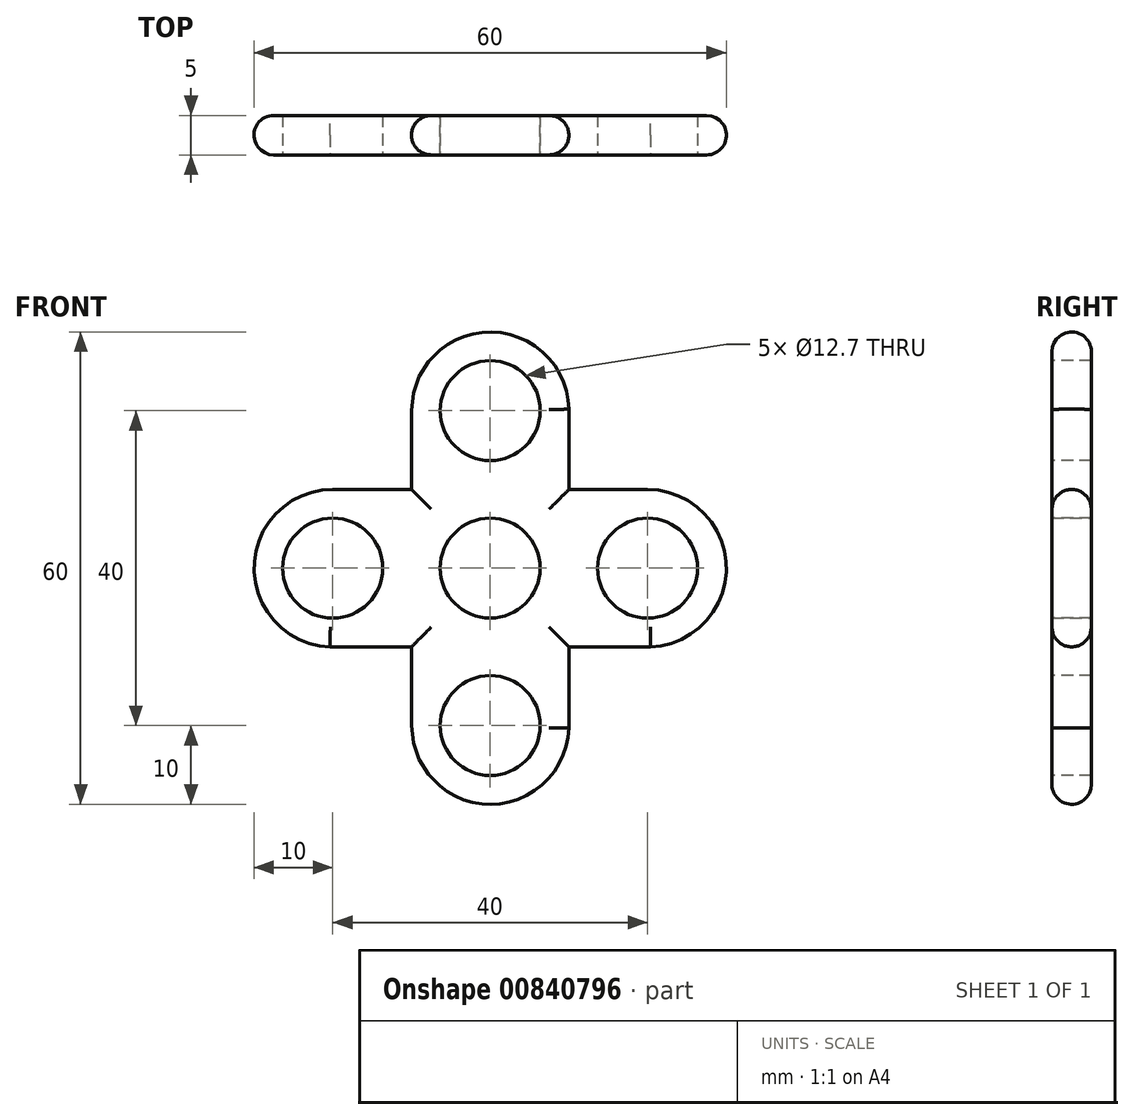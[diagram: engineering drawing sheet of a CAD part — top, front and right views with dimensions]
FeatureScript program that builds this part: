
annotation { "Feature Type Name" : "Feature", "Feature Type Description" : "" }
export const myFeature = defineFeature(function(context is Context, id is Id, definition is map)
    precondition{}
    {
        {
            var Q0;
            Q0=qCreatedBy(makeId("Front.planeOp"),FACE);
            var sketch = newSketch(context, id + "F0", { "sketchPlane" : qUnion([Q0])});
            skCircle(sketch, "E0", {"center": v(0, 0) * mm, "radius": 10 * mm});
            skCircle(sketch, "E1", {"center": v(0, 0) * mm, "radius": 6.35 * mm});
            skSolve(sketch);
        }
        {
            var Q0;
            Q0=makeQuery(id+"F0.imprint","IMPRINT",FACE,{"disambiguationData":[TD([[makeQuery(id+"F0.imprint","IMPRINT",EDGE,{"derivedFrom":sQuery(id+"F0.wireOp",EDGE,"E0")}),1.0]])]});
            extrude(context, id + "F1", {"entities" : qUnion([Q0]), "depth" : 5 * mm, "offsetDistance" : 25 * mm});
        }
        {
            var Q0;
            Q0=makeQuery(id+"F1.opExtrude","CAP_FACE",FACE,{"disambiguationData":[OSD([sQuery(id+"F0.wireOp",EDGE,"E0"),sQuery(id+"F0.wireOp",EDGE,"E1")])],"isStart":false});
            var sketch = newSketch(context, id + "F2", { "sketchPlane" : qUnion([Q0])});
            skLineSegment(sketch, "E2", {"start": v(-10, 0) * mm, "end": v(-10, 30) * mm});
            skLineSegment(sketch, "E3", {"start": v(-10, 30) * mm, "end": v(10, 30) * mm});
            skLineSegment(sketch, "E4", {"start": v(10, 30) * mm, "end": v(10, 0) * mm});
            skLineSegment(sketch, "E5", {"start": v(10, 0) * mm, "end": v(10, -30) * mm});
            skLineSegment(sketch, "E6", {"start": v(10, -30) * mm, "end": v(-10, -30) * mm});
            skLineSegment(sketch, "E7", {"start": v(-10, -30) * mm, "end": v(-10, 0) * mm});
            skLineSegment(sketch, "E8", {"start": v(0, 10) * mm, "end": v(-30, 10) * mm});
            skLineSegment(sketch, "E9", {"start": v(-30, 10) * mm, "end": v(-30, -10) * mm});
            skLineSegment(sketch, "E10", {"start": v(-30, -10) * mm, "end": v(0, -10) * mm});
            skLineSegment(sketch, "E11", {"start": v(0, -10) * mm, "end": v(30, -10) * mm});
            skLineSegment(sketch, "E12", {"start": v(30, -10) * mm, "end": v(30, 10) * mm});
            skLineSegment(sketch, "E13", {"start": v(30, 10) * mm, "end": v(0, 10) * mm});
            skCircle(sketch, "E14", {"center": v(-20, 0) * mm, "radius": 10 * mm});
            skPoint(sketch, "E14.second.point", {"position": v(-30, 0) * mm});
            skPoint(sketch, "E14.third.point", {"position": v(-20.35, -10) * mm});
            skCircle(sketch, "E15", {"center": v(0, -20) * mm, "radius": 10 * mm});
            skPoint(sketch, "E15.second.point", {"position": v(0, -30) * mm});
            skPoint(sketch, "E15.third.point", {"position": v(10, -20.32) * mm});
            skCircle(sketch, "E16", {"center": v(20, 0) * mm, "radius": 10 * mm});
            skPoint(sketch, "E16.second.point", {"position": v(30, 0) * mm});
            skPoint(sketch, "E16.third.point", {"position": v(20.38, -10) * mm});
            skCircle(sketch, "E17", {"center": v(0, 20) * mm, "radius": 10 * mm});
            skPoint(sketch, "E17.second.point", {"position": v(0, 30) * mm});
            skPoint(sketch, "E17.third.point", {"position": v(10, 19.81) * mm});
            skCircle(sketch, "E18", {"center": v(-20, 0) * mm, "radius": 6.35 * mm});
            skCircle(sketch, "E19", {"center": v(0, 20) * mm, "radius": 6.35 * mm});
            skCircle(sketch, "E20", {"center": v(0, -20) * mm, "radius": 6.35 * mm});
            skCircle(sketch, "E21", {"center": v(20, 0) * mm, "radius": 6.35 * mm});
            skSolve(sketch);
        }
        {
            var Q0;
            Q0=makeQuery(id+"F2.imprint","IMPRINT",FACE,{"disambiguationData":[TD([[makeQuery(id+"F2.imprint","IMPRINT",EDGE,{"derivedFrom":sQuery(id+"F2.wireOp",EDGE,"E18")}),-1.0]])]});
            var Q1;
            Q1=makeQuery(id+"F2.imprint","IMPRINT",FACE,{"disambiguationData":[TD([[makeQuery(id+"F2.imprint","IMPRINT",EDGE,{"derivedFrom":sQuery(id+"F2.wireOp",EDGE,"E19")}),-1.0]])]});
            var Q2;
            Q2=makeQuery(id+"F2.imprint","IMPRINT",FACE,{"disambiguationData":[TD([[makeQuery(id+"F2.imprint","IMPRINT",EDGE,{"derivedFrom":sQuery(id+"F2.wireOp",EDGE,"E21")}),-1.0]])]});
            var Q3;
            Q3=makeQuery(id+"F2.imprint","IMPRINT",FACE,{"disambiguationData":[TD([[makeQuery(id+"F2.imprint","IMPRINT",EDGE,{"derivedFrom":sQuery(id+"F2.wireOp",EDGE,"E20")}),-1.0]])]});
            extrude(context, id + "F3", {"entities" : qUnion([Q0, Q1, Q2, Q3]), "operationType" : NewBodyOperationType.ADD, "oppositeDirection" : true, "depth" : 5 * mm, "offsetDistance" : 25 * mm});
        }
        {
            var Q0;
            Q0=makeQuery(id+"F3.boolean.opBoolean","MERGE",FACE,{"derivedFrom":[makeQuery(id+"F1.opExtrude","CAP_FACE",FACE,{"disambiguationData":[OSD([sQuery(id+"F0.wireOp",EDGE,"E0"),sQuery(id+"F0.wireOp",EDGE,"E1")])],"isStart":false}),makeQuery(id+"F3.opExtrude","CAP_FACE",FACE,{"disambiguationData":[OSD([sQuery(id+"F2.wireOp",EDGE,"E4"),sQuery(id+"F2.wireOp",EDGE,"E17"),sQuery(id+"F2.wireOp",EDGE,"E19")])],"isStart":true}),makeQuery(id+"F3.opExtrude","CAP_FACE",FACE,{"disambiguationData":[OSD([sQuery(id+"F2.wireOp",EDGE,"E5"),sQuery(id+"F2.wireOp",EDGE,"E15"),sQuery(id+"F2.wireOp",EDGE,"E20")])],"isStart":true}),makeQuery(id+"F3.opExtrude","CAP_FACE",FACE,{"disambiguationData":[OSD([sQuery(id+"F2.wireOp",EDGE,"E10"),sQuery(id+"F2.wireOp",EDGE,"E14"),sQuery(id+"F2.wireOp",EDGE,"E18")])],"isStart":true}),makeQuery(id+"F3.opExtrude","CAP_FACE",FACE,{"disambiguationData":[OSD([sQuery(id+"F2.wireOp",EDGE,"E11"),sQuery(id+"F2.wireOp",EDGE,"E16"),sQuery(id+"F2.wireOp",EDGE,"E21")])],"isStart":true})]});
            var sketch = newSketch(context, id + "F4", { "sketchPlane" : qUnion([Q0])});
            skLineSegment(sketch, "E22", {"start": v(-10, 0) * mm, "end": v(-10, 20) * mm});
            skLineSegment(sketch, "E23", {"start": v(0, 10) * mm, "end": v(-20, 10) * mm});
            skLineSegment(sketch, "E24", {"start": v(0, -10) * mm, "end": v(-20.35, -10) * mm});
            skLineSegment(sketch, "E25", {"start": v(-10, 0) * mm, "end": v(-10, -20) * mm});
            skLineSegment(sketch, "E26", {"start": v(10, 0) * mm, "end": v(10, -19.68) * mm});
            skLineSegment(sketch, "E27", {"start": v(0, -10) * mm, "end": v(19.62, -10) * mm});
            skLineSegment(sketch, "E28", {"start": v(10, 0) * mm, "end": v(10, 20.19) * mm});
            skLineSegment(sketch, "E29", {"start": v(0, 10) * mm, "end": v(20, 10) * mm});
            skSolve(sketch);
        }
        {
            var Q0;
            {var subQ0=sQuery(id+"F4.wireOp",EDGE,"E22");var subQ13=sQuery(id+"F4.wireOp",EDGE,"E23");var subQ14=makeQuery(id+"F4.imprint","INTERSECT",VERTEX,{"derivedFrom":[subQ0,subQ13]});Q0=makeQuery(id+"F4.imprint","IMPRINT",FACE,{"disambiguationData":[TD([[makeQuery(id+"F4.imprint","IMPRINT",EDGE,{"disambiguationData":[TD([[subQ14,-1.0]])],"derivedFrom":subQ13}),1.0]])]});}
            var Q1;
            {var subQ3=sQuery(id+"F0.wireOp",EDGE,"E0");var subQ4=sQuery(id+"F2.wireOp",EDGE,"E14");var subQ5=makeQuery(id+"F2.imprint","INTERSECT",VERTEX,{"derivedFrom":[sQuery(id+"F2.wireOp",EDGE,"E9"),subQ4]});var subQ6=sQuery(id+"F2.wireOp",EDGE,"E10");var subQ7=makeQuery(id+"F2.imprint","IMPRINT",EDGE,{"disambiguationData":[TD([[subQ5,-1.0],[makeQuery(id+"F2.imprint","INTERSECT",VERTEX,{"disambiguationData":[OD(0.0)],"derivedFrom":[subQ6,subQ4]}),1.0]])],"derivedFrom":subQ4});var subQ8=makeQuery(id+"F1.opExtrude","CAP_EDGE",EDGE,{"disambiguationData":[OSD([subQ3])],"isStart":false});var subQ9=makeQuery(id+"F2.imprint","IMPRINT",EDGE,{"disambiguationData":[TD([[makeQuery(id+"F2.imprint","INTERSECT",VERTEX,{"derivedFrom":[subQ8,sQuery(id+"F2.wireOp",EDGE,"E2"),subQ4]}),-1.0],[subQ5,1.0]])],"derivedFrom":subQ4});var subQ13=makeQuery(id+"F3.boolean.opBoolean","SPLIT",EDGE,{"disambiguationData":[TD([makeQuery(id+"F3.opExtrude","SWEPT_FACE",FACE,{"disambiguationData":[OSD([subQ4]),TDD([subQ9,subQ7])]})])],"derivedFrom":subQ8});Q1=makeQuery(id+"F4.imprint","IMPRINT",FACE,{"disambiguationData":[TD([[makeQuery(id+"F4.imprint","IMPRINT",EDGE,{"derivedFrom":subQ13}),-1.0]])]});}
            var Q2;
            {var subQ0=sQuery(id+"F4.wireOp",EDGE,"E22");var subQ10=sQuery(id+"F4.wireOp",EDGE,"E23");var subQ11=makeQuery(id+"F4.imprint","INTERSECT",VERTEX,{"derivedFrom":[subQ0,subQ10]});Q2=makeQuery(id+"F4.imprint","IMPRINT",FACE,{"disambiguationData":[TD([[makeQuery(id+"F4.imprint","IMPRINT",EDGE,{"disambiguationData":[TD([[subQ11,-1.0]])],"derivedFrom":subQ0}),-1.0]])]});}
            var Q3;
            {var subQ1=sQuery(id+"F2.wireOp",EDGE,"E14");var subQ2=sQuery(id+"F0.wireOp",EDGE,"E0");var subQ3=makeQuery(id+"F1.opExtrude","CAP_EDGE",EDGE,{"disambiguationData":[OSD([subQ2])],"isStart":false});var subQ4=sQuery(id+"F2.wireOp",EDGE,"E10");var subQ5=makeQuery(id+"F2.imprint","IMPRINT",EDGE,{"disambiguationData":[TD([[makeQuery(id+"F2.imprint","INTERSECT",VERTEX,{"derivedFrom":[subQ3,sQuery(id+"F2.wireOp",EDGE,"E7"),subQ1]}),1.0],[makeQuery(id+"F2.imprint","INTERSECT",VERTEX,{"disambiguationData":[OD(1.0)],"derivedFrom":[subQ4,subQ1]}),-1.0]])],"derivedFrom":subQ1});var subQ6=makeQuery(id+"F3.opExtrude","CAP_EDGE",EDGE,{"disambiguationData":[OSD([subQ1]),TDD([subQ5])],"isStart":true});Q3=makeQuery(id+"F4.imprint","IMPRINT",FACE,{"disambiguationData":[TD([[makeQuery(id+"F4.imprint","IMPRINT",EDGE,{"derivedFrom":subQ6}),-1.0]])]});}
            var Q4;
            {var subQ1=sQuery(id+"F0.wireOp",EDGE,"E0");var subQ4=sQuery(id+"F2.wireOp",EDGE,"E14");var subQ5=sQuery(id+"F2.wireOp",EDGE,"E10");var subQ6=makeQuery(id+"F1.opExtrude","CAP_EDGE",EDGE,{"disambiguationData":[OSD([subQ1])],"isStart":false});var subQ7=makeQuery(id+"F2.imprint","IMPRINT",EDGE,{"disambiguationData":[TD([[makeQuery(id+"F2.imprint","INTERSECT",VERTEX,{"derivedFrom":[subQ6,sQuery(id+"F2.wireOp",EDGE,"E7"),subQ4]}),1.0],[makeQuery(id+"F2.imprint","INTERSECT",VERTEX,{"disambiguationData":[OD(1.0)],"derivedFrom":[subQ5,subQ4]}),-1.0]])],"derivedFrom":subQ4});var subQ11=makeQuery(id+"F3.boolean.opBoolean","SPLIT",EDGE,{"disambiguationData":[TD([makeQuery(id+"F3.opExtrude","SWEPT_FACE",FACE,{"disambiguationData":[OSD([subQ4]),TDD([subQ7])]})])],"derivedFrom":subQ6});Q4=makeQuery(id+"F4.imprint","IMPRINT",FACE,{"disambiguationData":[TD([[makeQuery(id+"F4.imprint","IMPRINT",EDGE,{"derivedFrom":subQ11}),-1.0]])]});}
            var Q5;
            {var subQ0=sQuery(id+"F4.wireOp",EDGE,"E24");var subQ12=sQuery(id+"F4.wireOp",EDGE,"E25");var subQ13=makeQuery(id+"F4.imprint","INTERSECT",VERTEX,{"derivedFrom":[subQ0,subQ12]});Q5=makeQuery(id+"F4.imprint","IMPRINT",FACE,{"disambiguationData":[TD([[makeQuery(id+"F4.imprint","IMPRINT",EDGE,{"disambiguationData":[TD([[subQ13,-1.0]])],"derivedFrom":subQ12}),1.0]])]});}
            var Q6;
            {var subQ1=sQuery(id+"F2.wireOp",EDGE,"E15");var subQ2=sQuery(id+"F2.wireOp",EDGE,"E11");var subQ3=sQuery(id+"F0.wireOp",EDGE,"E0");var subQ4=makeQuery(id+"F1.opExtrude","CAP_EDGE",EDGE,{"disambiguationData":[OSD([subQ3])],"isStart":false});var subQ5=sQuery(id+"F2.wireOp",EDGE,"E5");var subQ6=makeQuery(id+"F2.imprint","IMPRINT",EDGE,{"disambiguationData":[TD([[makeQuery(id+"F2.imprint","INTERSECT",VERTEX,{"derivedFrom":[subQ4,subQ2,subQ1]}),1.0],[makeQuery(id+"F2.imprint","INTERSECT",VERTEX,{"disambiguationData":[OD(0.0)],"derivedFrom":[subQ5,subQ1]}),-1.0]])],"derivedFrom":subQ1});var subQ7=makeQuery(id+"F3.opExtrude","CAP_EDGE",EDGE,{"disambiguationData":[OSD([subQ1]),TDD([subQ6])],"isStart":true});Q6=makeQuery(id+"F4.imprint","IMPRINT",FACE,{"disambiguationData":[TD([[makeQuery(id+"F4.imprint","IMPRINT",EDGE,{"derivedFrom":subQ7}),-1.0]])]});}
            var Q7;
            {var subQ1=sQuery(id+"F0.wireOp",EDGE,"E0");var subQ2=sQuery(id+"F2.wireOp",EDGE,"E15");var subQ3=sQuery(id+"F2.wireOp",EDGE,"E5");var subQ4=sQuery(id+"F2.wireOp",EDGE,"E11");var subQ5=makeQuery(id+"F1.opExtrude","CAP_EDGE",EDGE,{"disambiguationData":[OSD([subQ1])],"isStart":false});var subQ6=makeQuery(id+"F2.imprint","IMPRINT",EDGE,{"disambiguationData":[TD([[makeQuery(id+"F2.imprint","INTERSECT",VERTEX,{"derivedFrom":[subQ5,subQ4,subQ2]}),1.0],[makeQuery(id+"F2.imprint","INTERSECT",VERTEX,{"disambiguationData":[OD(0.0)],"derivedFrom":[subQ3,subQ2]}),-1.0]])],"derivedFrom":subQ2});var subQ9=makeQuery(id+"F3.boolean.opBoolean","SPLIT",EDGE,{"disambiguationData":[TD([makeQuery(id+"F3.opExtrude","SWEPT_FACE",FACE,{"disambiguationData":[OSD([subQ2]),TDD([subQ6])]})])],"derivedFrom":subQ5});Q7=makeQuery(id+"F4.imprint","IMPRINT",FACE,{"disambiguationData":[TD([[makeQuery(id+"F4.imprint","IMPRINT",EDGE,{"derivedFrom":subQ9}),-1.0]])]});}
            var Q8;
            {var subQ1=sQuery(id+"F0.wireOp",EDGE,"E0");var subQ3=sQuery(id+"F2.wireOp",EDGE,"E5");var subQ4=sQuery(id+"F2.wireOp",EDGE,"E11");var subQ5=makeQuery(id+"F1.opExtrude","CAP_EDGE",EDGE,{"disambiguationData":[OSD([subQ1])],"isStart":false});var subQ6=sQuery(id+"F2.wireOp",EDGE,"E16");var subQ7=makeQuery(id+"F2.imprint","IMPRINT",EDGE,{"disambiguationData":[TD([[makeQuery(id+"F2.imprint","INTERSECT",VERTEX,{"derivedFrom":[subQ5,subQ3,subQ6]}),-1.0],[makeQuery(id+"F2.imprint","INTERSECT",VERTEX,{"disambiguationData":[OD(0.0)],"derivedFrom":[subQ4,subQ6]}),1.0]])],"derivedFrom":subQ6});var subQ8=makeQuery(id+"F3.opExtrude","CAP_EDGE",EDGE,{"disambiguationData":[OSD([subQ6]),TDD([subQ7])],"isStart":true});Q8=makeQuery(id+"F4.imprint","IMPRINT",FACE,{"disambiguationData":[TD([[makeQuery(id+"F4.imprint","IMPRINT",EDGE,{"derivedFrom":subQ8}),-1.0]])]});}
            var Q9;
            {var subQ0=sQuery(id+"F4.wireOp",EDGE,"E28");var subQ12=sQuery(id+"F4.wireOp",EDGE,"E29");var subQ13=makeQuery(id+"F4.imprint","INTERSECT",VERTEX,{"derivedFrom":[subQ0,subQ12]});Q9=makeQuery(id+"F4.imprint","IMPRINT",FACE,{"disambiguationData":[TD([[makeQuery(id+"F4.imprint","IMPRINT",EDGE,{"disambiguationData":[TD([[subQ13,-1.0]])],"derivedFrom":subQ12}),-1.0]])]});}
            var Q10;
            {var subQ1=sQuery(id+"F2.wireOp",EDGE,"E17");var subQ2=sQuery(id+"F2.wireOp",EDGE,"E4");var subQ3=sQuery(id+"F0.wireOp",EDGE,"E0");var subQ4=makeQuery(id+"F1.opExtrude","CAP_EDGE",EDGE,{"disambiguationData":[OSD([subQ3])],"isStart":false});var subQ5=makeQuery(id+"F2.imprint","IMPRINT",EDGE,{"disambiguationData":[TD([[makeQuery(id+"F2.imprint","INTERSECT",VERTEX,{"derivedFrom":[subQ4,sQuery(id+"F2.wireOp",EDGE,"E13"),subQ1]}),-1.0],[makeQuery(id+"F2.imprint","INTERSECT",VERTEX,{"disambiguationData":[OD(1.0)],"derivedFrom":[subQ2,subQ1]}),1.0]])],"derivedFrom":subQ1});var subQ11=makeQuery(id+"F3.boolean.opBoolean","SPLIT",EDGE,{"disambiguationData":[TD([makeQuery(id+"F3.opExtrude","SWEPT_FACE",FACE,{"disambiguationData":[OSD([subQ1]),TDD([subQ5])]})])],"derivedFrom":subQ4});Q10=makeQuery(id+"F4.imprint","IMPRINT",FACE,{"disambiguationData":[TD([[makeQuery(id+"F4.imprint","IMPRINT",EDGE,{"derivedFrom":subQ11}),-1.0]])]});}
            var Q11;
            {var subQ1=sQuery(id+"F2.wireOp",EDGE,"E17");var subQ2=sQuery(id+"F0.wireOp",EDGE,"E0");var subQ3=makeQuery(id+"F1.opExtrude","CAP_EDGE",EDGE,{"disambiguationData":[OSD([subQ2])],"isStart":false});var subQ4=sQuery(id+"F2.wireOp",EDGE,"E4");var subQ5=makeQuery(id+"F2.imprint","IMPRINT",EDGE,{"disambiguationData":[TD([[makeQuery(id+"F2.imprint","INTERSECT",VERTEX,{"derivedFrom":[subQ3,sQuery(id+"F2.wireOp",EDGE,"E13"),subQ1]}),-1.0],[makeQuery(id+"F2.imprint","INTERSECT",VERTEX,{"disambiguationData":[OD(1.0)],"derivedFrom":[subQ4,subQ1]}),1.0]])],"derivedFrom":subQ1});var subQ6=makeQuery(id+"F3.opExtrude","CAP_EDGE",EDGE,{"disambiguationData":[OSD([subQ1]),TDD([subQ5])],"isStart":true});Q11=makeQuery(id+"F4.imprint","IMPRINT",FACE,{"disambiguationData":[TD([[makeQuery(id+"F4.imprint","IMPRINT",EDGE,{"derivedFrom":subQ6}),-1.0]])]});}
            extrude(context, id + "F5", {"entities" : qUnion([Q0, Q1, Q2, Q3, Q4, Q5, Q6, Q7, Q8, Q9, Q10, Q11]), "operationType" : NewBodyOperationType.ADD, "oppositeDirection" : true, "depth" : 5 * mm, "offsetDistance" : 25 * mm});
        }
        {
            var Q0;
            Q0=makeQuery(id+"F5.opExtrude","CAP_EDGE",EDGE,{"disambiguationData":[OSD([sQuery(id+"F4.wireOp",EDGE,"E24")])],"isStart":false});
            var Q1;
            {var subQ0=sQuery(id+"F2.wireOp",EDGE,"E14");var subQ1=makeQuery(id+"F2.imprint","INTERSECT",VERTEX,{"derivedFrom":[sQuery(id+"F2.wireOp",EDGE,"E9"),subQ0]});Q1=makeQuery(id+"F3.opExtrude","CAP_EDGE",EDGE,{"disambiguationData":[OSD([subQ0]),TDD([makeQuery(id+"F2.imprint","IMPRINT",EDGE,{"disambiguationData":[TD([[makeQuery(id+"F2.imprint","INTERSECT",VERTEX,{"derivedFrom":[makeQuery(id+"F1.opExtrude","CAP_EDGE",EDGE,{"disambiguationData":[OSD([sQuery(id+"F0.wireOp",EDGE,"E0")])],"isStart":false}),sQuery(id+"F2.wireOp",EDGE,"E2"),subQ0]}),-1.0],[subQ1,1.0]])],"derivedFrom":subQ0}),makeQuery(id+"F2.imprint","IMPRINT",EDGE,{"disambiguationData":[TD([[subQ1,-1.0],[makeQuery(id+"F2.imprint","INTERSECT",VERTEX,{"disambiguationData":[OD(0.0)],"derivedFrom":[sQuery(id+"F2.wireOp",EDGE,"E10"),subQ0]}),1.0]])],"derivedFrom":subQ0})])],"isStart":false});}
            var Q2;
            Q2=makeQuery(id+"F5.opExtrude","CAP_EDGE",EDGE,{"disambiguationData":[OSD([sQuery(id+"F4.wireOp",EDGE,"E23")])],"isStart":false});
            var Q3;
            Q3=makeQuery(id+"F5.opExtrude","CAP_EDGE",EDGE,{"disambiguationData":[OSD([sQuery(id+"F4.wireOp",EDGE,"E22")])],"isStart":false});
            var Q4;
            {var subQ0=sQuery(id+"F2.wireOp",EDGE,"E17");var subQ1=makeQuery(id+"F2.imprint","INTERSECT",VERTEX,{"derivedFrom":[sQuery(id+"F2.wireOp",EDGE,"E3"),subQ0]});Q4=makeQuery(id+"F3.opExtrude","CAP_EDGE",EDGE,{"disambiguationData":[OSD([subQ0]),TDD([makeQuery(id+"F2.imprint","IMPRINT",EDGE,{"disambiguationData":[TD([[subQ1,1.0],[makeQuery(id+"F2.imprint","INTERSECT",VERTEX,{"disambiguationData":[OD(0.0)],"derivedFrom":[sQuery(id+"F2.wireOp",EDGE,"E4"),subQ0]}),-1.0]])],"derivedFrom":subQ0}),makeQuery(id+"F2.imprint","IMPRINT",EDGE,{"disambiguationData":[TD([[makeQuery(id+"F2.imprint","INTERSECT",VERTEX,{"derivedFrom":[makeQuery(id+"F1.opExtrude","CAP_EDGE",EDGE,{"disambiguationData":[OSD([sQuery(id+"F0.wireOp",EDGE,"E0")])],"isStart":false}),sQuery(id+"F2.wireOp",EDGE,"E8"),subQ0]}),1.0],[subQ1,-1.0]])],"derivedFrom":subQ0})])],"isStart":false});}
            var Q5;
            Q5=makeQuery(id+"F5.boolean.opBoolean","MERGE",EDGE,{"derivedFrom":[makeQuery(id+"F3.opExtrude","CAP_EDGE",EDGE,{"disambiguationData":[OSD([sQuery(id+"F2.wireOp",EDGE,"E4")])],"isStart":false}),makeQuery(id+"F5.opExtrude","CAP_EDGE",EDGE,{"disambiguationData":[OSD([sQuery(id+"F4.wireOp",EDGE,"E28")])],"isStart":false})]});
            var Q6;
            Q6=makeQuery(id+"F5.opExtrude","CAP_EDGE",EDGE,{"disambiguationData":[OSD([sQuery(id+"F4.wireOp",EDGE,"E29")])],"isStart":false});
            var Q7;
            {var subQ0=sQuery(id+"F2.wireOp",EDGE,"E16");var subQ1=makeQuery(id+"F2.imprint","INTERSECT",VERTEX,{"derivedFrom":[sQuery(id+"F2.wireOp",EDGE,"E12"),subQ0]});Q7=makeQuery(id+"F3.opExtrude","CAP_EDGE",EDGE,{"disambiguationData":[OSD([subQ0]),TDD([makeQuery(id+"F2.imprint","IMPRINT",EDGE,{"disambiguationData":[TD([[makeQuery(id+"F2.imprint","INTERSECT",VERTEX,{"derivedFrom":[makeQuery(id+"F1.opExtrude","CAP_EDGE",EDGE,{"disambiguationData":[OSD([sQuery(id+"F0.wireOp",EDGE,"E0")])],"isStart":false}),sQuery(id+"F2.wireOp",EDGE,"E4"),subQ0]}),1.0],[subQ1,-1.0]])],"derivedFrom":subQ0}),makeQuery(id+"F2.imprint","IMPRINT",EDGE,{"disambiguationData":[TD([[makeQuery(id+"F2.imprint","INTERSECT",VERTEX,{"disambiguationData":[OD(1.0)],"derivedFrom":[sQuery(id+"F2.wireOp",EDGE,"E11"),subQ0]}),-1.0],[subQ1,1.0]])],"derivedFrom":subQ0})])],"isStart":false});}
            var Q8;
            Q8=makeQuery(id+"F5.opExtrude","CAP_EDGE",EDGE,{"disambiguationData":[OSD([sQuery(id+"F4.wireOp",EDGE,"E27")])],"isStart":false});
            var Q9;
            Q9=makeQuery(id+"F5.boolean.opBoolean","MERGE",EDGE,{"derivedFrom":[makeQuery(id+"F3.opExtrude","CAP_EDGE",EDGE,{"disambiguationData":[OSD([sQuery(id+"F2.wireOp",EDGE,"E5")])],"isStart":false}),makeQuery(id+"F5.opExtrude","CAP_EDGE",EDGE,{"disambiguationData":[OSD([sQuery(id+"F4.wireOp",EDGE,"E26")])],"isStart":false})]});
            var Q10;
            {var subQ0=sQuery(id+"F2.wireOp",EDGE,"E15");var subQ1=makeQuery(id+"F2.imprint","INTERSECT",VERTEX,{"derivedFrom":[sQuery(id+"F2.wireOp",EDGE,"E6"),subQ0]});Q10=makeQuery(id+"F3.opExtrude","CAP_EDGE",EDGE,{"disambiguationData":[OSD([subQ0]),TDD([makeQuery(id+"F2.imprint","IMPRINT",EDGE,{"disambiguationData":[TD([[makeQuery(id+"F2.imprint","INTERSECT",VERTEX,{"derivedFrom":[makeQuery(id+"F1.opExtrude","CAP_EDGE",EDGE,{"disambiguationData":[OSD([sQuery(id+"F0.wireOp",EDGE,"E0")])],"isStart":false}),sQuery(id+"F2.wireOp",EDGE,"E10"),subQ0]}),-1.0],[subQ1,1.0]])],"derivedFrom":subQ0}),makeQuery(id+"F2.imprint","IMPRINT",EDGE,{"disambiguationData":[TD([[makeQuery(id+"F2.imprint","INTERSECT",VERTEX,{"disambiguationData":[OD(1.0)],"derivedFrom":[sQuery(id+"F2.wireOp",EDGE,"E5"),subQ0]}),1.0],[subQ1,-1.0]])],"derivedFrom":subQ0})])],"isStart":false});}
            var Q11;
            Q11=makeQuery(id+"F5.opExtrude","CAP_EDGE",EDGE,{"disambiguationData":[OSD([sQuery(id+"F4.wireOp",EDGE,"E25")])],"isStart":false});
            fillet(context, id + "F6", {"entities" : qUnion([Q0, Q1, Q2, Q3, Q4, Q5, Q6, Q7, Q8, Q9, Q10, Q11]), "radius" : 2.5 * mm, "tangentPropagation" : true, "allowEdgeOverflow" : false});
        }
        {
            var Q0;
            Q0=makeQuery(id+"F5.opExtrude","CAP_EDGE",EDGE,{"disambiguationData":[OSD([sQuery(id+"F4.wireOp",EDGE,"E24")])],"isStart":true});
            var Q1;
            {var subQ0=sQuery(id+"F2.wireOp",EDGE,"E14");var subQ1=makeQuery(id+"F2.imprint","INTERSECT",VERTEX,{"derivedFrom":[sQuery(id+"F2.wireOp",EDGE,"E9"),subQ0]});Q1=makeQuery(id+"F3.opExtrude","CAP_EDGE",EDGE,{"disambiguationData":[OSD([subQ0]),TDD([makeQuery(id+"F2.imprint","IMPRINT",EDGE,{"disambiguationData":[TD([[makeQuery(id+"F2.imprint","INTERSECT",VERTEX,{"derivedFrom":[makeQuery(id+"F1.opExtrude","CAP_EDGE",EDGE,{"disambiguationData":[OSD([sQuery(id+"F0.wireOp",EDGE,"E0")])],"isStart":false}),sQuery(id+"F2.wireOp",EDGE,"E2"),subQ0]}),-1.0],[subQ1,1.0]])],"derivedFrom":subQ0}),makeQuery(id+"F2.imprint","IMPRINT",EDGE,{"disambiguationData":[TD([[subQ1,-1.0],[makeQuery(id+"F2.imprint","INTERSECT",VERTEX,{"disambiguationData":[OD(0.0)],"derivedFrom":[sQuery(id+"F2.wireOp",EDGE,"E10"),subQ0]}),1.0]])],"derivedFrom":subQ0})])],"isStart":true});}
            var Q2;
            Q2=makeQuery(id+"F5.opExtrude","CAP_EDGE",EDGE,{"disambiguationData":[OSD([sQuery(id+"F4.wireOp",EDGE,"E23")])],"isStart":true});
            var Q3;
            Q3=makeQuery(id+"F5.opExtrude","CAP_EDGE",EDGE,{"disambiguationData":[OSD([sQuery(id+"F4.wireOp",EDGE,"E22")])],"isStart":true});
            var Q4;
            Q4=makeQuery(id+"F5.boolean.opBoolean","MERGE",EDGE,{"derivedFrom":[makeQuery(id+"F3.opExtrude","CAP_EDGE",EDGE,{"disambiguationData":[OSD([sQuery(id+"F2.wireOp",EDGE,"E4")])],"isStart":true}),makeQuery(id+"F5.opExtrude","CAP_EDGE",EDGE,{"disambiguationData":[OSD([sQuery(id+"F4.wireOp",EDGE,"E28")])],"isStart":true})]});
            var Q5;
            {var subQ0=sQuery(id+"F2.wireOp",EDGE,"E17");var subQ1=makeQuery(id+"F2.imprint","INTERSECT",VERTEX,{"derivedFrom":[sQuery(id+"F2.wireOp",EDGE,"E3"),subQ0]});Q5=makeQuery(id+"F3.opExtrude","CAP_EDGE",EDGE,{"disambiguationData":[OSD([subQ0]),TDD([makeQuery(id+"F2.imprint","IMPRINT",EDGE,{"disambiguationData":[TD([[subQ1,1.0],[makeQuery(id+"F2.imprint","INTERSECT",VERTEX,{"disambiguationData":[OD(0.0)],"derivedFrom":[sQuery(id+"F2.wireOp",EDGE,"E4"),subQ0]}),-1.0]])],"derivedFrom":subQ0}),makeQuery(id+"F2.imprint","IMPRINT",EDGE,{"disambiguationData":[TD([[makeQuery(id+"F2.imprint","INTERSECT",VERTEX,{"derivedFrom":[makeQuery(id+"F1.opExtrude","CAP_EDGE",EDGE,{"disambiguationData":[OSD([sQuery(id+"F0.wireOp",EDGE,"E0")])],"isStart":false}),sQuery(id+"F2.wireOp",EDGE,"E8"),subQ0]}),1.0],[subQ1,-1.0]])],"derivedFrom":subQ0})])],"isStart":true});}
            var Q6;
            Q6=makeQuery(id+"F5.opExtrude","CAP_EDGE",EDGE,{"disambiguationData":[OSD([sQuery(id+"F4.wireOp",EDGE,"E29")])],"isStart":true});
            var Q7;
            {var subQ0=sQuery(id+"F2.wireOp",EDGE,"E16");var subQ1=makeQuery(id+"F2.imprint","INTERSECT",VERTEX,{"derivedFrom":[sQuery(id+"F2.wireOp",EDGE,"E12"),subQ0]});Q7=makeQuery(id+"F3.opExtrude","CAP_EDGE",EDGE,{"disambiguationData":[OSD([subQ0]),TDD([makeQuery(id+"F2.imprint","IMPRINT",EDGE,{"disambiguationData":[TD([[makeQuery(id+"F2.imprint","INTERSECT",VERTEX,{"derivedFrom":[makeQuery(id+"F1.opExtrude","CAP_EDGE",EDGE,{"disambiguationData":[OSD([sQuery(id+"F0.wireOp",EDGE,"E0")])],"isStart":false}),sQuery(id+"F2.wireOp",EDGE,"E4"),subQ0]}),1.0],[subQ1,-1.0]])],"derivedFrom":subQ0}),makeQuery(id+"F2.imprint","IMPRINT",EDGE,{"disambiguationData":[TD([[makeQuery(id+"F2.imprint","INTERSECT",VERTEX,{"disambiguationData":[OD(1.0)],"derivedFrom":[sQuery(id+"F2.wireOp",EDGE,"E11"),subQ0]}),-1.0],[subQ1,1.0]])],"derivedFrom":subQ0})])],"isStart":true});}
            var Q8;
            Q8=makeQuery(id+"F5.opExtrude","CAP_EDGE",EDGE,{"disambiguationData":[OSD([sQuery(id+"F4.wireOp",EDGE,"E25")])],"isStart":true});
            var Q9;
            {var subQ0=sQuery(id+"F2.wireOp",EDGE,"E15");var subQ1=makeQuery(id+"F2.imprint","INTERSECT",VERTEX,{"derivedFrom":[sQuery(id+"F2.wireOp",EDGE,"E6"),subQ0]});Q9=makeQuery(id+"F3.opExtrude","CAP_EDGE",EDGE,{"disambiguationData":[OSD([subQ0]),TDD([makeQuery(id+"F2.imprint","IMPRINT",EDGE,{"disambiguationData":[TD([[makeQuery(id+"F2.imprint","INTERSECT",VERTEX,{"derivedFrom":[makeQuery(id+"F1.opExtrude","CAP_EDGE",EDGE,{"disambiguationData":[OSD([sQuery(id+"F0.wireOp",EDGE,"E0")])],"isStart":false}),sQuery(id+"F2.wireOp",EDGE,"E10"),subQ0]}),-1.0],[subQ1,1.0]])],"derivedFrom":subQ0}),makeQuery(id+"F2.imprint","IMPRINT",EDGE,{"disambiguationData":[TD([[makeQuery(id+"F2.imprint","INTERSECT",VERTEX,{"disambiguationData":[OD(1.0)],"derivedFrom":[sQuery(id+"F2.wireOp",EDGE,"E5"),subQ0]}),1.0],[subQ1,-1.0]])],"derivedFrom":subQ0})])],"isStart":true});}
            var Q10;
            Q10=makeQuery(id+"F5.boolean.opBoolean","MERGE",EDGE,{"derivedFrom":[makeQuery(id+"F3.opExtrude","CAP_EDGE",EDGE,{"disambiguationData":[OSD([sQuery(id+"F2.wireOp",EDGE,"E5")])],"isStart":true}),makeQuery(id+"F5.opExtrude","CAP_EDGE",EDGE,{"disambiguationData":[OSD([sQuery(id+"F4.wireOp",EDGE,"E26")])],"isStart":true})]});
            var Q11;
            Q11=makeQuery(id+"F5.opExtrude","CAP_EDGE",EDGE,{"disambiguationData":[OSD([sQuery(id+"F4.wireOp",EDGE,"E27")])],"isStart":true});
            fillet(context, id + "F7", {"entities" : qUnion([Q0, Q1, Q2, Q3, Q4, Q5, Q6, Q7, Q8, Q9, Q10, Q11]), "radius" : 2.5 * mm, "tangentPropagation" : true, "allowEdgeOverflow" : false});
        }
    });
